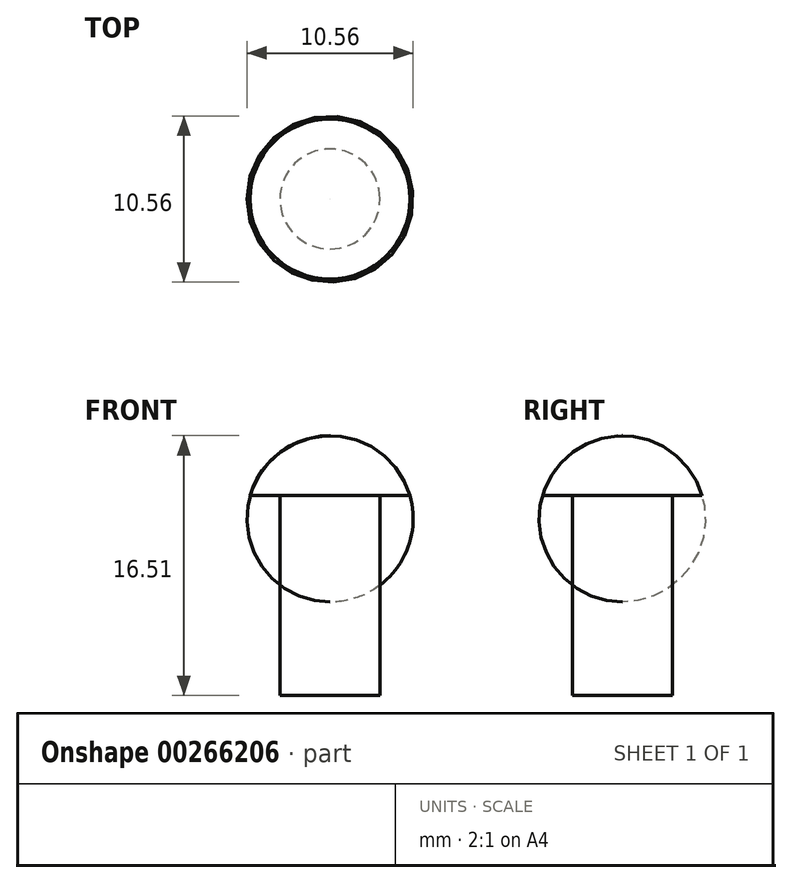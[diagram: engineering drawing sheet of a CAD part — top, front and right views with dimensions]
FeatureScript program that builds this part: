
annotation { "Feature Type Name" : "Feature", "Feature Type Description" : "" }
export const myFeature = defineFeature(function(context is Context, id is Id, definition is map)
    precondition{}
    {
        {
            var Q0;
            Q0=qCreatedBy(makeId("Front.planeOp"),FACE);
            var sketch = newSketch(context, id + "F0", { "sketchPlane" : qUnion([Q0])});
            skLineSegment(sketch, "E0", {"start": v(0, 0) * mm, "end": v(0, 16.51) * mm});
            skLineSegment(sketch, "E1", {"start": v(0, 16.51) * mm, "end": v(0, 0) * mm});
            skLineSegment(sketch, "E2", {"start": v(0, 0) * mm, "end": v(3.17, 0) * mm});
            skLineSegment(sketch, "E3", {"start": v(3.17, 0) * mm, "end": v(3.17, 12.7) * mm});
            skLineSegment(sketch, "E4", {"start": v(3.17, 12.7) * mm, "end": v(5.08, 12.7) * mm});
            skArc(sketch, "E5", {"start": v(5.08, 12.7) * mm, "mid": v(3.18, 15.45) * mm, "end": v(0, 16.51) * mm});
            skSolve(sketch);
        }
        {
            var Q0;
            Q0 = qSketchRegion(id + "F0", true);
            var Q1;
            Q1=sQuery(id+"F0.wireOp",EDGE,"E1");
            revolve(context, id + "F1", {"entities" : qUnion([Q0]), "axis" : qUnion([Q1]), "revolveType" : RevolveType.FULL});
        }
    });
